# Revit family: BuroSeating_Polo Stool
name_source: partatom
category: Furniture
units: mm (PartAtom-declared; Revit-internal decimal feet)

## family parameters
Always vertical = Yes
Cut with Voids When Loaded = No
OmniClass Number = 23.40.70.14.64.11
OmniClass Title = Office Furniture
Room Calculation Point = No
Shared = No
Work Plane-Based = No

## types (1)
- Buro Polo Stool
    Assembly Code = E2020
    BottomLiftMaterial = BuroSeating_Aluminium_Black
    CastorCoverMaterial = BuroSeating_Aluminium_Brushed_Black
    CastorMaterial = BuroSeating_Aluminium_Black
    CastorWheelMaterial = BuroSeating_Aluminium_Black
    Default Elevation = 0 mm  [stored 0 ft]
    Description = Buro Polo Stool
    FeetMaterial = BuroSeating_Aluminium_Brushed_Black
    FootRingMaterial = BuroSeating_Aluminium_Black
    Manufacturer = Buro Seating
    Model = 142-PU3-AT
    NominalDepth = 580 mm  [stored 1.90289 ft]
    NominalSeatHeight = 615-860h
    NominalWidth = 580 mm  [stored 1.90289 ft]
    ProductGroup = Polo
    ProductPageURL AU = https://buroseating.com
    ProductPageURL NZ = https://buroseating.co.nz
    ProductRange = Buro
    SeatDiameter = 385 mm  [stored 1.26312 ft]
    SeatMaterial = BuroSeating_Leather_Black
    SeatTiltMaterial = BuroSeating_Aluminium_Black
    TopLiftMaterial = BuroSeating_Aluminium_Black
    Type Comments = Seat Height 615-860mm High
    URL = https://buroseating.co.nz
    URL AU = https://buroseating.com
    WarrantyDescription = Full 5 year guarantee (excluding upholstery)

note: [stored X ft] marks values corroborated as IEEE doubles in the binary element streams (Revit-internal decimal feet)

## geometry (parser evidence)
native form markers: Sweep x5
no freeform markers — native parametric forms only
